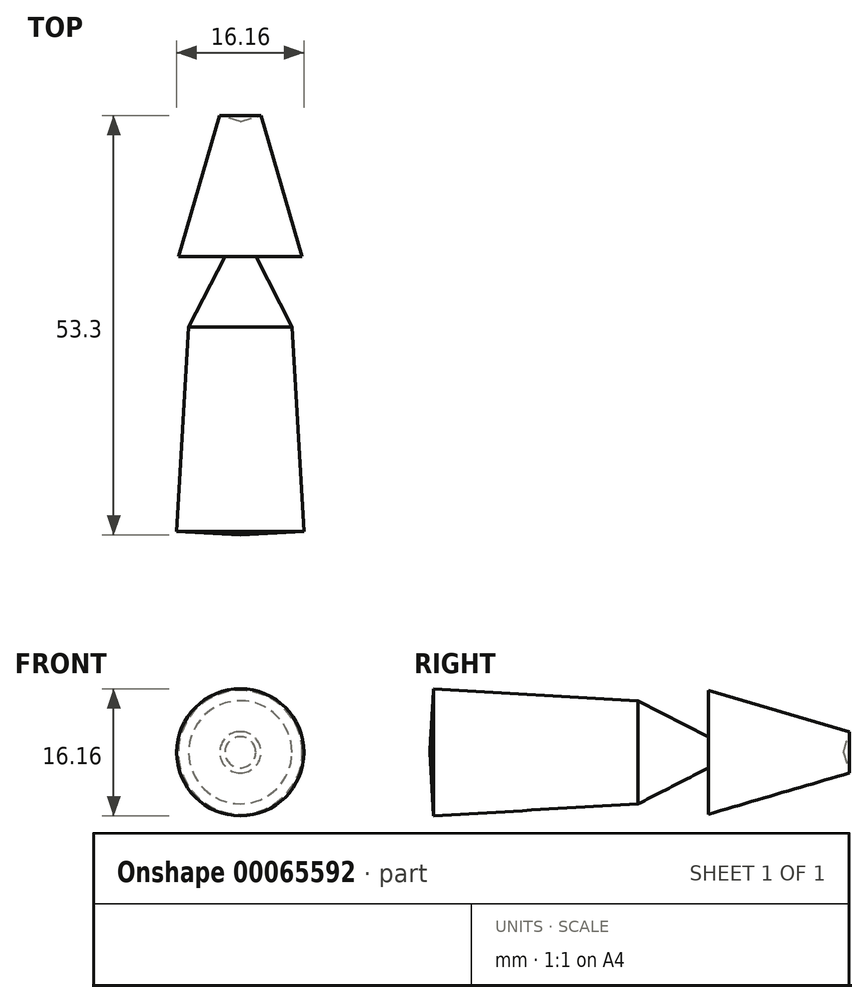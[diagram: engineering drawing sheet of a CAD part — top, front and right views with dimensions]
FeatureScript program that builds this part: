
annotation { "Feature Type Name" : "Feature", "Feature Type Description" : "" }
export const myFeature = defineFeature(function(context is Context, id is Id, definition is map)
    precondition{}
    {
        {
            var Q0;
            Q0=qCreatedBy(makeId("Top.planeOp"),FACE);
            var sketch = newSketch(context, id + "F0", { "sketchPlane" : qUnion([Q0])});
            skLineSegment(sketch, "E0", {"start": v(-8.08, -23.9) * mm, "end": v(-6.55, 2.07) * mm});
            skLineSegment(sketch, "E1", {"start": v(-6.55, 2.07) * mm, "end": v(-1.96, 11.02) * mm});
            skLineSegment(sketch, "E2", {"start": v(-1.96, 11.02) * mm, "end": v(-7.86, 11.02) * mm});
            skLineSegment(sketch, "E3", {"start": v(-7.86, 11.02) * mm, "end": v(-2.62, 28.92) * mm});
            skLineSegment(sketch, "E4", {"start": v(-2.62, 28.92) * mm, "end": v(0, 28.16) * mm});
            skLineSegment(sketch, "E5", {"start": v(-8.08, -23.9) * mm, "end": v(0, -24.38) * mm});
            skLineSegment(sketch, "E6", {"start": v(0, -24.38) * mm, "end": v(0, 28.16) * mm});
            skSolve(sketch);
        }
        {
            var Q0;
            Q0=makeQuery(id+"F0.imprint","IMPRINT",FACE,{"disambiguationData":[TD([[makeQuery(id+"F0.imprint","IMPRINT",EDGE,{"derivedFrom":sQuery(id+"F0.wireOp",EDGE,"E0")}),-1.0]])]});
            var Q1;
            Q1=sQuery(id+"F0.wireOp",EDGE,"E6");
            revolve(context, id + "F1", {"entities" : qUnion([Q0]), "axis" : qUnion([Q1]), "revolveType" : RevolveType.FULL});
        }
    });
